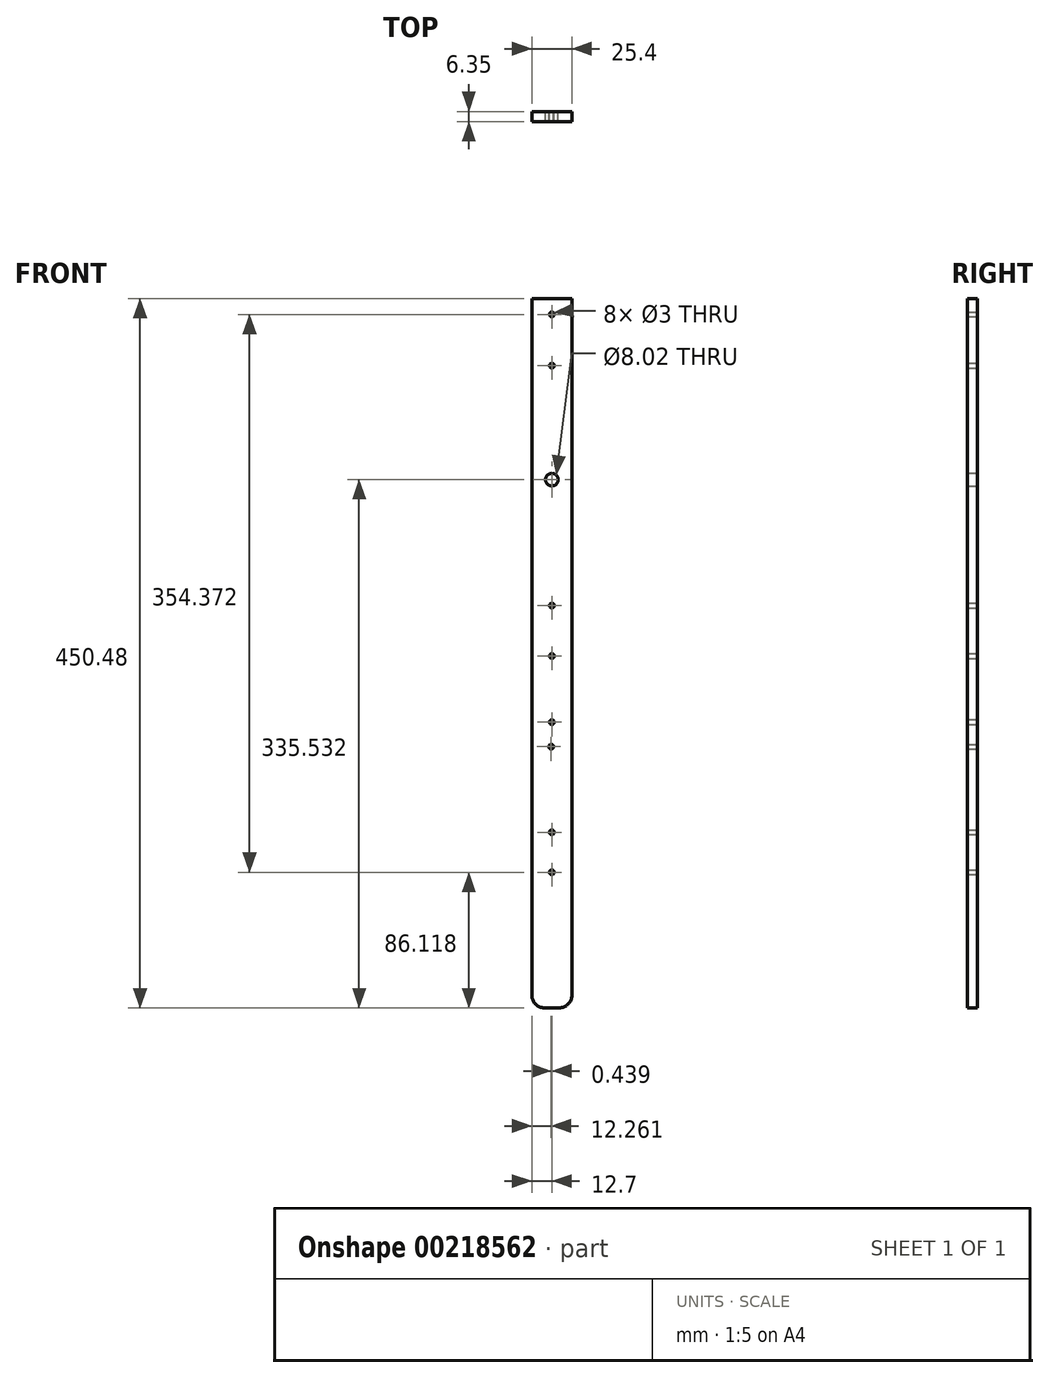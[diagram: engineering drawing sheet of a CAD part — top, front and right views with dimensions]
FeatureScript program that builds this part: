
annotation { "Feature Type Name" : "Feature", "Feature Type Description" : "" }
export const myFeature = defineFeature(function(context is Context, id is Id, definition is map)
    precondition{}
    {
        {
            var Q0;
            Q0=qCreatedBy(makeId("Front.planeOp"),FACE);
            var sketch = newSketch(context, id + "F0", { "sketchPlane" : qUnion([Q0])});
            skCircle(sketch, "E0", {"center": v(0, -85.45) * mm, "radius": 1.5 * mm});
            skCircle(sketch, "E1", {"center": v(-0.44, -31.05) * mm, "radius": 1.5 * mm});
            skCircle(sketch, "E2", {"center": v(0, 26.55) * mm, "radius": 1.5 * mm});
            skLineSegment(sketch, "E3.top", {"start": v(-4.69, -196.97) * mm, "end": v(4.69, -196.97) * mm});
            skLineSegment(sketch, "E3.left", {"start": v(-12.7, 249.87) * mm, "end": v(-12.7, -188.95) * mm});
            skLineSegment(sketch, "E3.right", {"start": v(12.7, 251.2) * mm, "end": v(12.7, -188.95) * mm});
            skPoint(sketch, "E4.visualSharp", {"position": v(12.7, 256.22) * mm});
            skPoint(sketch, "E5.visualSharp", {"position": v(12.7, -196.97) * mm});
            skArc(sketch, "E5.filletArc", {"start": v(4.69, -196.97) * mm, "mid": v(10.35, -194.62) * mm, "end": v(12.7, -188.95) * mm});
            skPoint(sketch, "E6.visualSharp", {"position": v(-12.7, -196.97) * mm});
            skArc(sketch, "E6.filletArc", {"start": v(-12.7, -188.95) * mm, "mid": v(-10.35, -194.62) * mm, "end": v(-4.69, -196.97) * mm});
            skCircle(sketch, "E7", {"center": v(0, 58.56) * mm, "radius": 1.5 * mm});
            skLineSegment(sketch, "E8", {"start": v(0, 26.55) * mm, "end": v(0, 99.81) * mm, "construction": true});
            skLineSegment(sketch, "E9", {"start": v(0, 99.81) * mm, "end": v(0, -85.45) * mm, "construction": true});
            skLineSegment(sketch, "E10", {"start": v(0, -85.45) * mm, "end": v(0, -201.73) * mm, "construction": true});
            skCircle(sketch, "E11", {"center": v(0, 243.52) * mm, "radius": 1.5 * mm});
            skCircle(sketch, "E12", {"center": v(0, -110.85) * mm, "radius": 1.5 * mm});
            skCircle(sketch, "E13", {"center": v(0, -15.45) * mm, "radius": 1.5 * mm});
            skLineSegment(sketch, "E14", {"start": v(0, 58.56) * mm, "end": v(0, 424.12) * mm});
            skCircle(sketch, "E15", {"center": v(0, 210.96) * mm, "radius": 1.5 * mm});
            skCircle(sketch, "E16", {"center": v(0, 138.56) * mm, "radius": 4 * mm});
            skLineSegment(sketch, "E17.bottom", {"start": v(-7.5, 253.51) * mm, "end": v(6.54, 253.51) * mm});
            skLineSegment(sketch, "E18", {"start": v(-7.5, 253.51) * mm, "end": v(-12.7, 253.51) * mm});
            skLineSegment(sketch, "E19", {"start": v(-12.7, 253.51) * mm, "end": v(-12.7, 249.87) * mm});
            skLineSegment(sketch, "E20.MirrorCS", {"start": v(7.5, 253.51) * mm, "end": v(12.7, 253.51) * mm});
            skLineSegment(sketch, "E21", {"start": v(12.7, 251.2) * mm, "end": v(12.7, 253.51) * mm});
            skLineSegment(sketch, "E22", {"start": v(7.5, 253.51) * mm, "end": v(6.54, 253.51) * mm});
            skSolve(sketch);
        }
        {
            var Q0;
            Q0=makeQuery(id+"F0.imprint","IMPRINT",FACE,{"disambiguationData":[TD([[makeQuery(id+"F0.imprint","IMPRINT",EDGE,{"derivedFrom":sQuery(id+"F0.wireOp",EDGE,"E0")}),-1.0]])]});
            extrude(context, id + "F1", {"entities" : qUnion([Q0]), "depth" : 6.35 * mm});
        }
    });
